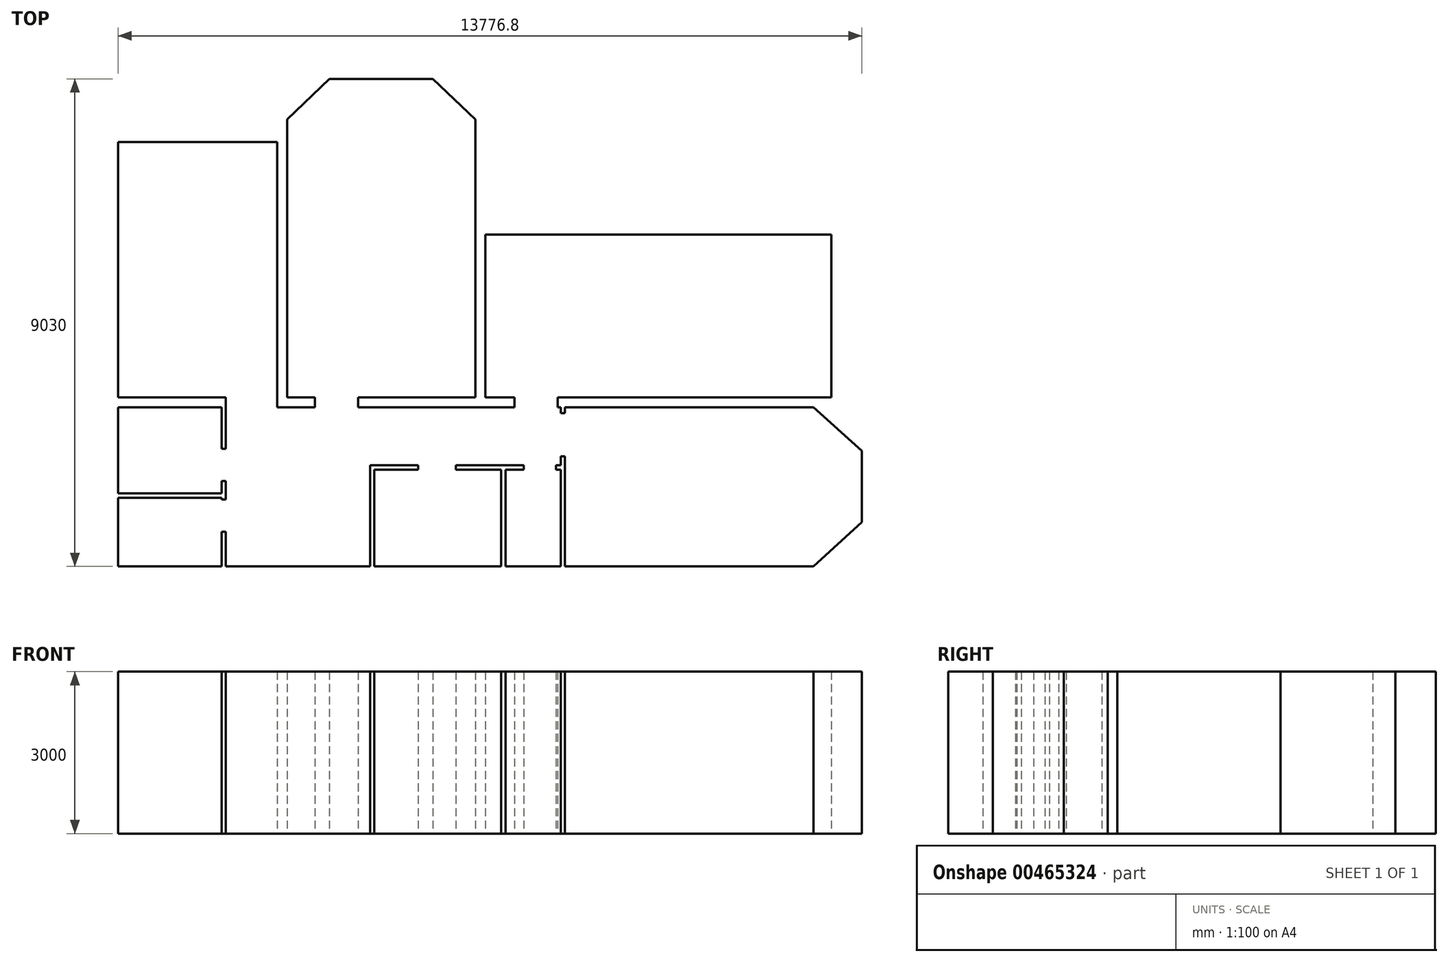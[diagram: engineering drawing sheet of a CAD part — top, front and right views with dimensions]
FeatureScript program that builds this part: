
annotation { "Feature Type Name" : "Feature", "Feature Type Description" : "" }
export const myFeature = defineFeature(function(context is Context, id is Id, definition is map)
    precondition{}
    {
        {
            var Q0;
            Q0=qCreatedBy(makeId("Top.planeOp"),FACE);
            var sketch = newSketch(context, id + "F0", { "sketchPlane" : qUnion([Q0])});
            skLineSegment(sketch, "E0.bottom", {"start": v(-953.2, 0) * mm, "end": v(-2950, 0) * mm});
            skLineSegment(sketch, "E0.top", {"start": v(0, 4730) * mm, "end": v(-2950, 4730) * mm});
            skLineSegment(sketch, "E0.left", {"start": v(0, 0) * mm, "end": v(0, 4730) * mm});
            skLineSegment(sketch, "E0.right", {"start": v(-2950, 0) * mm, "end": v(-2950, 4730) * mm});
            skLineSegment(sketch, "E1.bottom", {"start": v(180, 0) * mm, "end": v(698.35, 0) * mm});
            skLineSegment(sketch, "E1.left", {"start": v(180, 0) * mm, "end": v(180, 5150) * mm});
            skLineSegment(sketch, "E1.right", {"start": v(3670, 0) * mm, "end": v(3670, 5150) * mm});
            skLineSegment(sketch, "E2", {"start": v(180, 5150) * mm, "end": v(960, 5900) * mm});
            skLineSegment(sketch, "E3", {"start": v(3670, 5150) * mm, "end": v(2880, 5900) * mm});
            skLineSegment(sketch, "E4", {"start": v(2880, 5900) * mm, "end": v(960, 5900) * mm});
            skLineSegment(sketch, "E5.top", {"start": v(0, -3130) * mm, "end": v(-953.2, -3130) * mm});
            skLineSegment(sketch, "E5.right", {"start": v(-953.2, -180) * mm, "end": v(-953.2, -950.22) * mm});
            skLineSegment(sketch, "E6", {"start": v(0, -180) * mm, "end": v(698.35, -180) * mm});
            skLineSegment(sketch, "E7", {"start": v(5246.8, -180) * mm, "end": v(5246.8, -288.16) * mm});
            skLineSegment(sketch, "E8", {"start": v(5246.8, -1258.42) * mm, "end": v(5161.04, -1258.42) * mm});
            skLineSegment(sketch, "E9", {"start": v(1716.8, -1258.42) * mm, "end": v(1716.8, -3130) * mm});
            skLineSegment(sketch, "E10", {"start": v(1716.8, -3130) * mm, "end": v(0, -3130) * mm});
            skLineSegment(sketch, "E11", {"start": v(1796.8, -1338.42) * mm, "end": v(2606.75, -1338.42) * mm});
            skLineSegment(sketch, "E12", {"start": v(4146.8, -1338.42) * mm, "end": v(4146.8, -3130) * mm});
            skLineSegment(sketch, "E13", {"start": v(4146.8, -3130) * mm, "end": v(1796.8, -3130) * mm});
            skLineSegment(sketch, "E14", {"start": v(1796.8, -3130) * mm, "end": v(1796.8, -1338.42) * mm});
            skLineSegment(sketch, "E15", {"start": v(4226.8, -1338.42) * mm, "end": v(4561.04, -1338.42) * mm});
            skLineSegment(sketch, "E16", {"start": v(5246.8, -1338.42) * mm, "end": v(5246.8, -3130) * mm});
            skLineSegment(sketch, "E17", {"start": v(5246.8, -3130) * mm, "end": v(4226.8, -3130) * mm});
            skLineSegment(sketch, "E18", {"start": v(4226.8, -3130) * mm, "end": v(4226.8, -1338.42) * mm});
            skLineSegment(sketch, "E19", {"start": v(3850, 0) * mm, "end": v(4391.34, 0) * mm});
            skLineSegment(sketch, "E20", {"start": v(10260, 0) * mm, "end": v(10260, 3020) * mm});
            skLineSegment(sketch, "E21", {"start": v(10260, 3020) * mm, "end": v(3850, 3020) * mm});
            skLineSegment(sketch, "E22", {"start": v(3850, 3020) * mm, "end": v(3850, 0) * mm});
            skLineSegment(sketch, "E23", {"start": v(5326.8, -180) * mm, "end": v(9926.8, -180) * mm});
            skLineSegment(sketch, "E24", {"start": v(9926.8, -3130) * mm, "end": v(5326.8, -3130) * mm});
            skLineSegment(sketch, "E25", {"start": v(5326.8, -3130) * mm, "end": v(5326.8, -1088.16) * mm});
            skLineSegment(sketch, "E26", {"start": v(-1033.2, -180) * mm, "end": v(-1033.2, -950.22) * mm});
            skLineSegment(sketch, "E27", {"start": v(-1033.2, -1780) * mm, "end": v(-2950, -1780) * mm});
            skLineSegment(sketch, "E28", {"start": v(-2950, -1780) * mm, "end": v(-2950, -180) * mm});
            skLineSegment(sketch, "E29", {"start": v(-2950, -180) * mm, "end": v(-1033.2, -180) * mm});
            skLineSegment(sketch, "E30", {"start": v(-1033.2, -1860) * mm, "end": v(-1033.2, -1889.7) * mm});
            skLineSegment(sketch, "E31", {"start": v(-1033.2, -3130) * mm, "end": v(-2950, -3130) * mm});
            skLineSegment(sketch, "E32", {"start": v(-2950, -3130) * mm, "end": v(-2950, -1860) * mm});
            skLineSegment(sketch, "E33", {"start": v(-2950, -1860) * mm, "end": v(-1033.2, -1860) * mm});
            skLineSegment(sketch, "E34", {"start": v(9926.8, -180) * mm, "end": v(10826.8, -990) * mm});
            skLineSegment(sketch, "E35", {"start": v(9926.8, -3130) * mm, "end": v(10826.8, -2310) * mm});
            skLineSegment(sketch, "E36", {"start": v(10826.8, -2310) * mm, "end": v(10826.8, -990) * mm});
            skLineSegment(sketch, "E37", {"start": v(-953.2, -180) * mm, "end": v(-953.2, 0) * mm});
            skLineSegment(sketch, "E38", {"start": v(0, -180) * mm, "end": v(0, 0) * mm});
            skLineSegment(sketch, "E39", {"start": v(5191.34, -180) * mm, "end": v(5191.34, 0) * mm});
            skLineSegment(sketch, "E40", {"start": v(4391.34, 0) * mm, "end": v(4391.34, -180) * mm});
            skLineSegment(sketch, "E41.trimOffspring", {"start": v(5191.34, 0) * mm, "end": v(10260, 0) * mm});
            skLineSegment(sketch, "E42.trimOffspring", {"start": v(5191.34, -180) * mm, "end": v(5246.8, -180) * mm});
            skLineSegment(sketch, "E43", {"start": v(5246.8, -288.16) * mm, "end": v(5326.8, -288.16) * mm});
            skLineSegment(sketch, "E44", {"start": v(5326.8, -1088.16) * mm, "end": v(5246.8, -1088.16) * mm});
            skLineSegment(sketch, "E45.trimOffspring", {"start": v(5326.8, -288.16) * mm, "end": v(5326.8, -180) * mm});
            skLineSegment(sketch, "E46.trimOffspring", {"start": v(5246.8, -1088.16) * mm, "end": v(5246.8, -1258.42) * mm});
            skLineSegment(sketch, "E47", {"start": v(5161.04, -1338.42) * mm, "end": v(5161.04, -1258.42) * mm});
            skLineSegment(sketch, "E48", {"start": v(4561.04, -1258.42) * mm, "end": v(4561.04, -1338.42) * mm});
            skLineSegment(sketch, "E49.trimOffspring", {"start": v(4561.04, -1258.42) * mm, "end": v(3306.75, -1258.42) * mm});
            skLineSegment(sketch, "E50.trimOffspring", {"start": v(5161.04, -1338.42) * mm, "end": v(5246.8, -1338.42) * mm});
            skLineSegment(sketch, "E51", {"start": v(3306.75, -1258.42) * mm, "end": v(3306.75, -1338.42) * mm});
            skLineSegment(sketch, "E52", {"start": v(2606.75, -1338.42) * mm, "end": v(2606.75, -1258.42) * mm});
            skLineSegment(sketch, "E53.trimOffspring", {"start": v(3306.75, -1338.42) * mm, "end": v(4146.8, -1338.42) * mm});
            skLineSegment(sketch, "E54.trimOffspring", {"start": v(2606.75, -1258.42) * mm, "end": v(1716.8, -1258.42) * mm});
            skLineSegment(sketch, "E55", {"start": v(698.35, 0) * mm, "end": v(698.35, -180) * mm});
            skLineSegment(sketch, "E56", {"start": v(1498.35, -180) * mm, "end": v(1498.35, 0) * mm});
            skLineSegment(sketch, "E57.trimOffspring", {"start": v(1498.35, 0) * mm, "end": v(3670, 0) * mm});
            skLineSegment(sketch, "E58.trimOffspring", {"start": v(1498.35, -180) * mm, "end": v(4391.34, -180) * mm});
            skLineSegment(sketch, "E59", {"start": v(-1033.2, -1550.22) * mm, "end": v(-953.2, -1550.22) * mm});
            skPoint(sketch, "E59.endSnap0", {"position": v(-953.2, -1655) * mm});
            skLineSegment(sketch, "E60", {"start": v(-953.2, -950.22) * mm, "end": v(-1033.2, -950.22) * mm});
            skLineSegment(sketch, "E61.trimOffspring", {"start": v(-1033.2, -1550.22) * mm, "end": v(-1033.2, -1780) * mm});
            skLineSegment(sketch, "E62.trimOffspring", {"start": v(-953.2, -1550.22) * mm, "end": v(-953.2, -1889.7) * mm});
            skLineSegment(sketch, "E63", {"start": v(-1033.2, -1889.7) * mm, "end": v(-953.2, -1889.7) * mm});
            skLineSegment(sketch, "E64", {"start": v(-953.2, -2489.7) * mm, "end": v(-1033.2, -2489.7) * mm});
            skLineSegment(sketch, "E65.trimOffspring", {"start": v(-953.2, -2489.7) * mm, "end": v(-953.2, -3130) * mm});
            skLineSegment(sketch, "E66.trimOffspring", {"start": v(-1033.2, -2489.7) * mm, "end": v(-1033.2, -3130) * mm});
            skSolve(sketch);
        }
        {
            var Q0;
            Q0 = qSketchRegion(id + "F0", true);
            extrude(context, id + "F1", {"entities" : qUnion([Q0]), "depth" : 3000 * mm});
        }
    });
